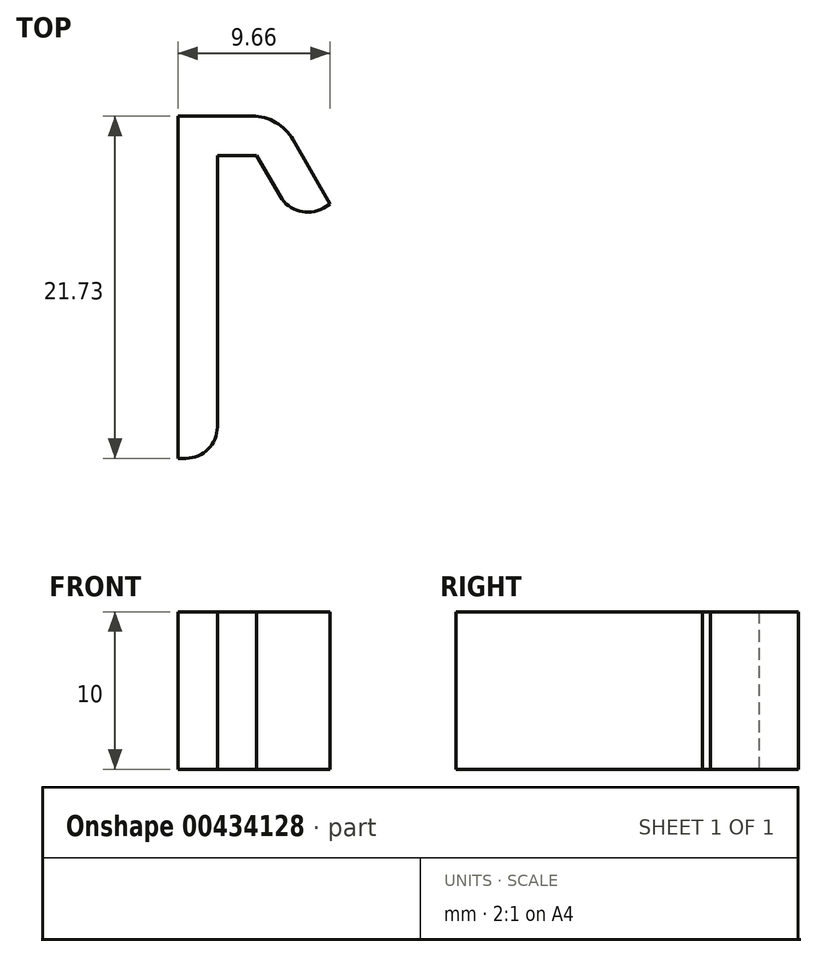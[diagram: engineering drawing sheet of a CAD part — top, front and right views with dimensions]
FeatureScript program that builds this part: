
annotation { "Feature Type Name" : "Feature", "Feature Type Description" : "" }
export const myFeature = defineFeature(function(context is Context, id is Id, definition is map)
    precondition{}
    {
        {
            var Q0;
            Q0=qCreatedBy(makeId("Top.planeOp"),FACE);
            var sketch = newSketch(context, id + "F0", { "sketchPlane" : qUnion([Q0])});
            skLineSegment(sketch, "E0", {"start": v(-7.58, 2) * mm, "end": v(-7.58, 19.23) * mm});
            skLineSegment(sketch, "E1", {"start": v(-7.58, 19.23) * mm, "end": v(-5.08, 19.23) * mm});
            skLineSegment(sketch, "E2", {"start": v(-5.08, 19.23) * mm, "end": v(-3.58, 16.64) * mm});
            skLineSegment(sketch, "E3.0", {"start": v(-3.64, 21.73) * mm, "end": v(-0.42, 16.15) * mm});
            skLineSegment(sketch, "E3.1", {"start": v(-10.08, 21.73) * mm, "end": v(-3.64, 21.73) * mm});
            skLineSegment(sketch, "E3.2", {"start": v(-10.08, 0) * mm, "end": v(-10.08, 21.73) * mm});
            skLineSegment(sketch, "E4", {"start": v(-0.85, 15.9) * mm, "end": v(-0.42, 16.15) * mm});
            skLineSegment(sketch, "E5", {"start": v(-10.08, 0) * mm, "end": v(-9.58, 0) * mm});
            skPoint(sketch, "E6.visualSharp", {"position": v(-2.58, 14.9) * mm});
            skArc(sketch, "E6.filletArc", {"start": v(-3.58, 16.64) * mm, "mid": v(-2.37, 15.7) * mm, "end": v(-0.85, 15.9) * mm});
            skPoint(sketch, "E7.visualSharp", {"position": v(-7.58, 0) * mm});
            skArc(sketch, "E7.filletArc", {"start": v(-9.58, 0) * mm, "mid": v(-8.17, 0.59) * mm, "end": v(-7.58, 2) * mm});
            skSolve(sketch);
        }
        {
            var Q0;
            Q0 = qSketchRegion(id + "F0", true);
            var Q1;
            Q1=makeQuery(id+"F0.imprint","IMPRINT",FACE,{"disambiguationData":[TD([[makeQuery(id+"F0.imprint","IMPRINT",EDGE,{"derivedFrom":sQuery(id+"F0.wireOp",EDGE,"E0")}),1.0]])]});
            extrude(context, id + "F1", {"entities" : qUnion([Q0, Q1]), "depth" : 10 * mm});
        }
        {
            var Q0;
            Q0=makeQuery(id+"F1.opExtrude","SWEPT_EDGE",EDGE,{"disambiguationData":[OSD([sQuery(id+"F0.wireOp",EDGE,"E3.0"),sQuery(id+"F0.wireOp",EDGE,"E3.1")])]});
            fillet(context, id + "F2", {"entities" : qUnion([Q0]), "radius" : 3 * mm, "tangentPropagation" : true, "allowEdgeOverflow" : false});
        }
    });
